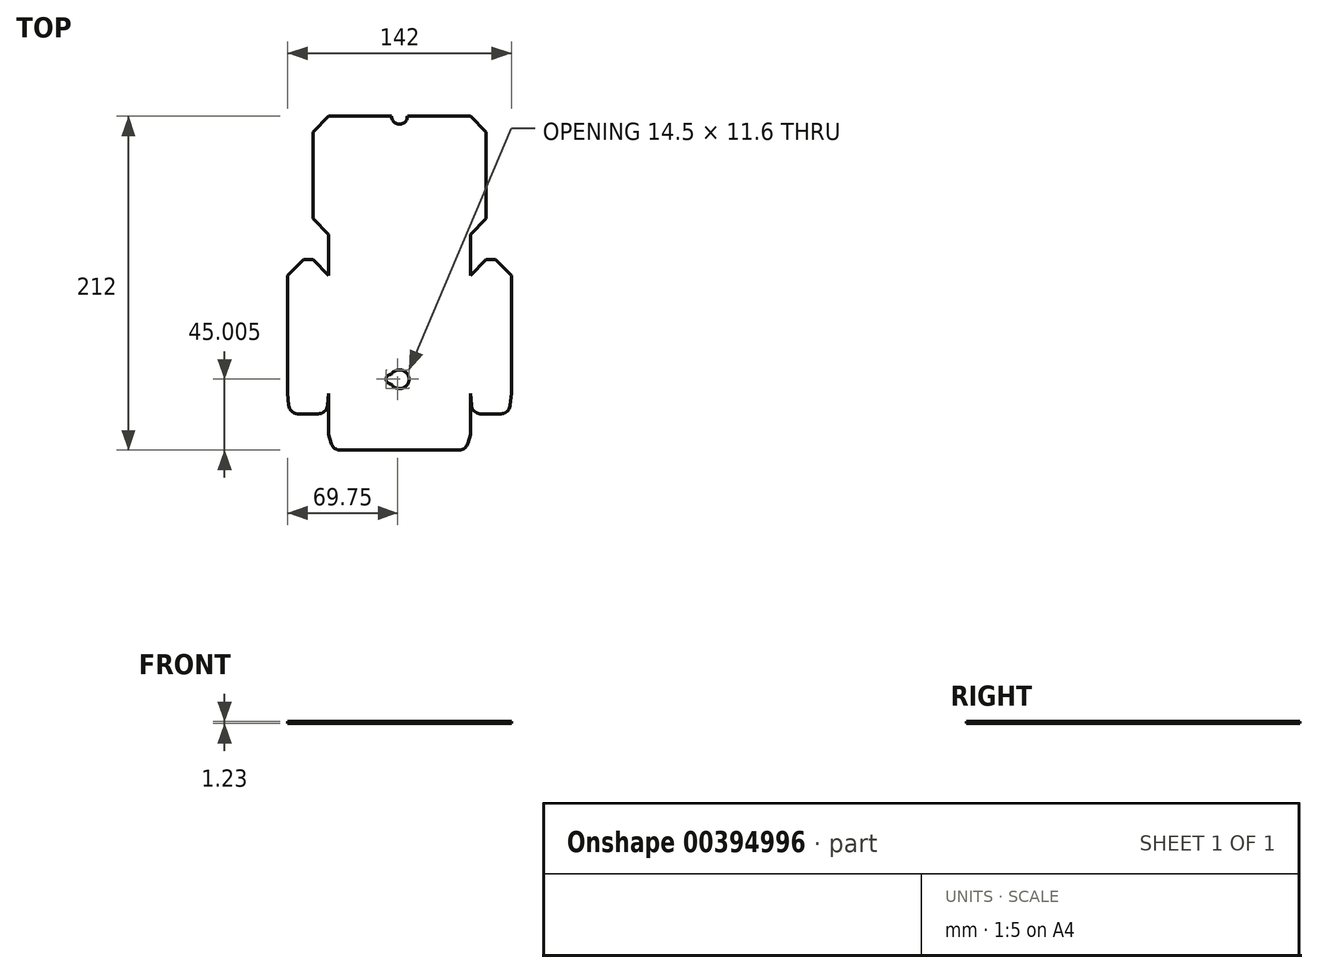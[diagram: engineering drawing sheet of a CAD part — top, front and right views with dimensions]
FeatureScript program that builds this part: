
annotation { "Feature Type Name" : "Feature", "Feature Type Description" : "" }
export const myFeature = defineFeature(function(context is Context, id is Id, definition is map)
    precondition{}
    {
        {
            var Q0;
            Q0=qCreatedBy(makeId("Top.planeOp"),FACE);
            var sketch = newSketch(context, id + "F0", { "sketchPlane" : qUnion([Q0])});
            skLineSegment(sketch, "E0", {"start": v(-70.76, -47.2) * mm, "end": v(-70.1, -54.72) * mm});
            skLineSegment(sketch, "E1", {"start": v(-70.1, -54.72) * mm, "end": v(-69.92, -55.75) * mm});
            skLineSegment(sketch, "E2", {"start": v(-69.92, -55.75) * mm, "end": v(-69.56, -56.73) * mm});
            skLineSegment(sketch, "E3", {"start": v(-69.56, -56.73) * mm, "end": v(-69.04, -57.64) * mm});
            skLineSegment(sketch, "E4", {"start": v(-69.04, -57.64) * mm, "end": v(-68.37, -58.44) * mm});
            skLineSegment(sketch, "E5", {"start": v(-68.37, -58.44) * mm, "end": v(-67.57, -59.11) * mm});
            skLineSegment(sketch, "E6", {"start": v(-67.57, -59.11) * mm, "end": v(-66.66, -59.63) * mm});
            skLineSegment(sketch, "E7", {"start": v(-66.66, -59.63) * mm, "end": v(-65.68, -60) * mm});
            skLineSegment(sketch, "E8", {"start": v(-65.68, -60) * mm, "end": v(-64.65, -60.17) * mm});
            skLineSegment(sketch, "E9", {"start": v(-64.65, -60.17) * mm, "end": v(-64.12, -60.2) * mm});
            skLineSegment(sketch, "E10", {"start": v(-64.12, -60.2) * mm, "end": v(-51.4, -60.2) * mm});
            skLineSegment(sketch, "E11", {"start": v(-51.4, -60.2) * mm, "end": v(-50.35, -60.1) * mm});
            skLineSegment(sketch, "E12", {"start": v(-50.35, -60.1) * mm, "end": v(-49.34, -59.83) * mm});
            skLineSegment(sketch, "E13", {"start": v(-49.34, -59.83) * mm, "end": v(-48.4, -59.4) * mm});
            skLineSegment(sketch, "E14", {"start": v(-48.4, -59.4) * mm, "end": v(-47.54, -58.8) * mm});
            skLineSegment(sketch, "E15", {"start": v(-47.54, -58.8) * mm, "end": v(-46.8, -58.05) * mm});
            skLineSegment(sketch, "E16", {"start": v(-46.8, -58.05) * mm, "end": v(-46.2, -57.2) * mm});
            skLineSegment(sketch, "E17", {"start": v(-46.2, -57.2) * mm, "end": v(-45.76, -56.25) * mm});
            skLineSegment(sketch, "E18", {"start": v(-45.76, -56.25) * mm, "end": v(-45.49, -55.24) * mm});
            skLineSegment(sketch, "E19", {"start": v(-45.49, -55.24) * mm, "end": v(-45.42, -54.72) * mm});
            skLineSegment(sketch, "E20", {"start": v(-45.42, -54.72) * mm, "end": v(-44.76, -47.2) * mm});
            skLineSegment(sketch, "E21", {"start": v(-44.76, -47.2) * mm, "end": v(-44.76, -73.2) * mm});
            skLineSegment(sketch, "E22", {"start": v(-44.76, -73.2) * mm, "end": v(-43.27, -78.75) * mm});
            skLineSegment(sketch, "E23", {"start": v(-43.27, -78.75) * mm, "end": v(-42.91, -79.73) * mm});
            skLineSegment(sketch, "E24", {"start": v(-42.91, -79.73) * mm, "end": v(-42.4, -80.64) * mm});
            skLineSegment(sketch, "E25", {"start": v(-42.4, -80.64) * mm, "end": v(-41.72, -81.44) * mm});
            skLineSegment(sketch, "E26", {"start": v(-41.72, -81.44) * mm, "end": v(-40.92, -82.11) * mm});
            skLineSegment(sketch, "E27", {"start": v(-40.92, -82.11) * mm, "end": v(-40.01, -82.63) * mm});
            skLineSegment(sketch, "E28", {"start": v(-40.01, -82.63) * mm, "end": v(-39.03, -83) * mm});
            skLineSegment(sketch, "E29", {"start": v(-39.03, -83) * mm, "end": v(-38, -83.17) * mm});
            skLineSegment(sketch, "E30", {"start": v(-38, -83.17) * mm, "end": v(-37.48, -83.2) * mm});
            skLineSegment(sketch, "E31", {"start": v(-37.48, -83.2) * mm, "end": v(37.96, -83.2) * mm});
            skLineSegment(sketch, "E32", {"start": v(37.96, -83.2) * mm, "end": v(39, -83.1) * mm});
            skLineSegment(sketch, "E33", {"start": v(39, -83.1) * mm, "end": v(40, -82.83) * mm});
            skLineSegment(sketch, "E34", {"start": v(40, -82.83) * mm, "end": v(40.96, -82.4) * mm});
            skLineSegment(sketch, "E35", {"start": v(40.96, -82.4) * mm, "end": v(41.81, -81.8) * mm});
            skLineSegment(sketch, "E36", {"start": v(41.81, -81.8) * mm, "end": v(42.55, -81.05) * mm});
            skLineSegment(sketch, "E37", {"start": v(42.55, -81.05) * mm, "end": v(43.15, -80.2) * mm});
            skLineSegment(sketch, "E38", {"start": v(43.15, -80.2) * mm, "end": v(43.6, -79.25) * mm});
            skLineSegment(sketch, "E39", {"start": v(43.6, -79.25) * mm, "end": v(43.75, -78.75) * mm});
            skLineSegment(sketch, "E40", {"start": v(43.75, -78.75) * mm, "end": v(45.24, -73.2) * mm});
            skLineSegment(sketch, "E41", {"start": v(45.24, -73.2) * mm, "end": v(45.24, -47.2) * mm});
            skLineSegment(sketch, "E42", {"start": v(45.24, -47.2) * mm, "end": v(45.9, -54.72) * mm});
            skLineSegment(sketch, "E43", {"start": v(45.9, -54.72) * mm, "end": v(46.08, -55.75) * mm});
            skLineSegment(sketch, "E44", {"start": v(46.08, -55.75) * mm, "end": v(46.44, -56.73) * mm});
            skLineSegment(sketch, "E45", {"start": v(46.44, -56.73) * mm, "end": v(46.96, -57.64) * mm});
            skLineSegment(sketch, "E46", {"start": v(46.96, -57.64) * mm, "end": v(47.63, -58.44) * mm});
            skLineSegment(sketch, "E47", {"start": v(47.63, -58.44) * mm, "end": v(48.43, -59.11) * mm});
            skLineSegment(sketch, "E48", {"start": v(48.43, -59.11) * mm, "end": v(49.34, -59.63) * mm});
            skLineSegment(sketch, "E49", {"start": v(49.34, -59.63) * mm, "end": v(50.32, -60) * mm});
            skLineSegment(sketch, "E50", {"start": v(50.32, -60) * mm, "end": v(51.35, -60.17) * mm});
            skLineSegment(sketch, "E51", {"start": v(51.35, -60.17) * mm, "end": v(51.88, -60.2) * mm});
            skLineSegment(sketch, "E52", {"start": v(51.88, -60.2) * mm, "end": v(64.6, -60.2) * mm});
            skLineSegment(sketch, "E53", {"start": v(64.6, -60.2) * mm, "end": v(65.65, -60.1) * mm});
            skLineSegment(sketch, "E54", {"start": v(65.65, -60.1) * mm, "end": v(66.66, -59.83) * mm});
            skLineSegment(sketch, "E55", {"start": v(66.66, -59.83) * mm, "end": v(67.6, -59.4) * mm});
            skLineSegment(sketch, "E56", {"start": v(67.6, -59.4) * mm, "end": v(68.46, -58.8) * mm});
            skLineSegment(sketch, "E57", {"start": v(68.46, -58.8) * mm, "end": v(69.2, -58.05) * mm});
            skLineSegment(sketch, "E58", {"start": v(69.2, -58.05) * mm, "end": v(69.8, -57.2) * mm});
            skLineSegment(sketch, "E59", {"start": v(69.8, -57.2) * mm, "end": v(70.24, -56.25) * mm});
            skLineSegment(sketch, "E60", {"start": v(70.24, -56.25) * mm, "end": v(70.51, -55.24) * mm});
            skLineSegment(sketch, "E61", {"start": v(70.51, -55.24) * mm, "end": v(70.58, -54.72) * mm});
            skLineSegment(sketch, "E62", {"start": v(70.58, -54.72) * mm, "end": v(71.24, -47.2) * mm});
            skLineSegment(sketch, "E63", {"start": v(71.24, -47.2) * mm, "end": v(71.24, 27.8) * mm});
            skLineSegment(sketch, "E64", {"start": v(71.24, 27.8) * mm, "end": v(61.24, 37.8) * mm});
            skLineSegment(sketch, "E65", {"start": v(61.24, 37.8) * mm, "end": v(55.24, 37.8) * mm});
            skLineSegment(sketch, "E66", {"start": v(55.24, 37.8) * mm, "end": v(45.24, 27.8) * mm});
            skLineSegment(sketch, "E67", {"start": v(45.24, 27.8) * mm, "end": v(45.24, 53.8) * mm});
            skLineSegment(sketch, "E68", {"start": v(45.24, 53.8) * mm, "end": v(55.24, 63.8) * mm});
            skLineSegment(sketch, "E69", {"start": v(55.24, 63.8) * mm, "end": v(55.24, 118.8) * mm});
            skLineSegment(sketch, "E70", {"start": v(55.24, 118.8) * mm, "end": v(45.24, 128.8) * mm});
            skLineSegment(sketch, "E71", {"start": v(45.24, 128.8) * mm, "end": v(5.24, 128.8) * mm});
            skLineSegment(sketch, "E72", {"start": v(5.24, 128.8) * mm, "end": v(5.16, 127.94) * mm});
            skLineSegment(sketch, "E73", {"start": v(5.16, 127.94) * mm, "end": v(4.94, 127.1) * mm});
            skLineSegment(sketch, "E74", {"start": v(4.94, 127.1) * mm, "end": v(4.57, 126.3) * mm});
            skLineSegment(sketch, "E75", {"start": v(4.57, 126.3) * mm, "end": v(4.07, 125.6) * mm});
            skLineSegment(sketch, "E76", {"start": v(4.07, 125.6) * mm, "end": v(3.45, 124.97) * mm});
            skLineSegment(sketch, "E77", {"start": v(3.45, 124.97) * mm, "end": v(2.74, 124.47) * mm});
            skLineSegment(sketch, "E78", {"start": v(2.74, 124.47) * mm, "end": v(1.95, 124.1) * mm});
            skLineSegment(sketch, "E79", {"start": v(1.95, 124.1) * mm, "end": v(1.1, 123.88) * mm});
            skLineSegment(sketch, "E80", {"start": v(1.1, 123.88) * mm, "end": v(0.24, 123.8) * mm});
            skLineSegment(sketch, "E81", {"start": v(0.24, 123.8) * mm, "end": v(-0.63, 123.88) * mm});
            skLineSegment(sketch, "E82", {"start": v(-0.63, 123.88) * mm, "end": v(-1.47, 124.1) * mm});
            skLineSegment(sketch, "E83", {"start": v(-1.47, 124.1) * mm, "end": v(-2.26, 124.47) * mm});
            skLineSegment(sketch, "E84", {"start": v(-2.26, 124.47) * mm, "end": v(-2.97, 124.97) * mm});
            skLineSegment(sketch, "E85", {"start": v(-2.97, 124.97) * mm, "end": v(-3.6, 125.6) * mm});
            skLineSegment(sketch, "E86", {"start": v(-3.6, 125.6) * mm, "end": v(-4.1, 126.3) * mm});
            skLineSegment(sketch, "E87", {"start": v(-4.1, 126.3) * mm, "end": v(-4.46, 127.1) * mm});
            skLineSegment(sketch, "E88", {"start": v(-4.46, 127.1) * mm, "end": v(-4.68, 127.94) * mm});
            skLineSegment(sketch, "E89", {"start": v(-4.68, 127.94) * mm, "end": v(-4.76, 128.8) * mm});
            skLineSegment(sketch, "E90", {"start": v(-4.76, 128.8) * mm, "end": v(-44.76, 128.8) * mm});
            skLineSegment(sketch, "E91", {"start": v(-44.76, 128.8) * mm, "end": v(-54.76, 118.8) * mm});
            skLineSegment(sketch, "E92", {"start": v(-54.76, 118.8) * mm, "end": v(-54.76, 63.8) * mm});
            skLineSegment(sketch, "E93", {"start": v(-54.76, 63.8) * mm, "end": v(-44.76, 53.8) * mm});
            skLineSegment(sketch, "E94", {"start": v(-44.76, 53.8) * mm, "end": v(-44.76, 27.8) * mm});
            skLineSegment(sketch, "E95", {"start": v(-44.76, 27.8) * mm, "end": v(-54.76, 37.8) * mm});
            skLineSegment(sketch, "E96", {"start": v(-54.76, 37.8) * mm, "end": v(-60.76, 37.8) * mm});
            skLineSegment(sketch, "E97", {"start": v(-60.76, 37.8) * mm, "end": v(-70.76, 27.8) * mm});
            skLineSegment(sketch, "E98", {"start": v(-70.76, 27.8) * mm, "end": v(-70.76, -47.2) * mm});
            skLineSegment(sketch, "E99", {"start": v(-70.76, 27.8) * mm, "end": v(-44.76, 27.8) * mm, "construction": true});
            skLineSegment(sketch, "E100", {"start": v(45.24, -47.2) * mm, "end": v(71.24, -47.2) * mm, "construction": true});
            skLineSegment(sketch, "E101", {"start": v(45.24, 27.8) * mm, "end": v(71.24, 27.8) * mm, "construction": true});
            skLineSegment(sketch, "E102", {"start": v(-70.76, -47.2) * mm, "end": v(-44.76, -47.2) * mm, "construction": true});
            skLineSegment(sketch, "E103", {"start": v(-44.76, 27.8) * mm, "end": v(45.24, 27.8) * mm, "construction": true});
            skLineSegment(sketch, "E104", {"start": v(-44.76, 53.8) * mm, "end": v(45.24, 53.8) * mm, "construction": true});
            skLineSegment(sketch, "E105", {"start": v(-44.76, -73.2) * mm, "end": v(45.24, -73.2) * mm, "construction": true});
            skLineSegment(sketch, "E106", {"start": v(-44.76, -47.2) * mm, "end": v(45.24, -47.2) * mm, "construction": true});
            skLineSegment(sketch, "E107", {"start": v(-44.76, 53.8) * mm, "end": v(-44.76, 128.8) * mm, "construction": true});
            skLineSegment(sketch, "E108", {"start": v(45.24, -47.2) * mm, "end": v(45.24, 27.8) * mm, "construction": true});
            skLineSegment(sketch, "E109", {"start": v(45.24, 53.8) * mm, "end": v(45.24, 128.8) * mm, "construction": true});
            skLineSegment(sketch, "E110", {"start": v(-44.76, -47.2) * mm, "end": v(-44.76, 27.8) * mm, "construction": true});
            skSolve(sketch);
        }
        {
            var Q0;
            Q0 = qSketchRegion(id + "F0", true);
            extrude(context, id + "F1", {"entities" : qUnion([Q0]), "depth" : 1.23 * mm});
        }
        {
            var Q0;
            Q0=makeQuery(id+"F1.opExtrude","CAP_FACE",FACE,{"disambiguationData":[OSD([sQuery(id+"F0.wireOp",EDGE,"E0"),sQuery(id+"F0.wireOp",EDGE,"E1"),sQuery(id+"F0.wireOp",EDGE,"E2"),sQuery(id+"F0.wireOp",EDGE,"E3"),sQuery(id+"F0.wireOp",EDGE,"E4"),sQuery(id+"F0.wireOp",EDGE,"E5"),sQuery(id+"F0.wireOp",EDGE,"E6"),sQuery(id+"F0.wireOp",EDGE,"E7"),sQuery(id+"F0.wireOp",EDGE,"E8"),sQuery(id+"F0.wireOp",EDGE,"E9"),sQuery(id+"F0.wireOp",EDGE,"E10"),sQuery(id+"F0.wireOp",EDGE,"E11"),sQuery(id+"F0.wireOp",EDGE,"E12"),sQuery(id+"F0.wireOp",EDGE,"E13"),sQuery(id+"F0.wireOp",EDGE,"E14"),sQuery(id+"F0.wireOp",EDGE,"E15"),sQuery(id+"F0.wireOp",EDGE,"E16"),sQuery(id+"F0.wireOp",EDGE,"E17"),sQuery(id+"F0.wireOp",EDGE,"E18"),sQuery(id+"F0.wireOp",EDGE,"E19"),sQuery(id+"F0.wireOp",EDGE,"E20"),sQuery(id+"F0.wireOp",EDGE,"E21"),sQuery(id+"F0.wireOp",EDGE,"E22"),sQuery(id+"F0.wireOp",EDGE,"E23"),sQuery(id+"F0.wireOp",EDGE,"E24"),sQuery(id+"F0.wireOp",EDGE,"E25"),sQuery(id+"F0.wireOp",EDGE,"E26"),sQuery(id+"F0.wireOp",EDGE,"E27"),sQuery(id+"F0.wireOp",EDGE,"E28"),sQuery(id+"F0.wireOp",EDGE,"E29"),sQuery(id+"F0.wireOp",EDGE,"E30"),sQuery(id+"F0.wireOp",EDGE,"E31"),sQuery(id+"F0.wireOp",EDGE,"E32"),sQuery(id+"F0.wireOp",EDGE,"E33"),sQuery(id+"F0.wireOp",EDGE,"E34"),sQuery(id+"F0.wireOp",EDGE,"E35"),sQuery(id+"F0.wireOp",EDGE,"E36"),sQuery(id+"F0.wireOp",EDGE,"E37"),sQuery(id+"F0.wireOp",EDGE,"E38"),sQuery(id+"F0.wireOp",EDGE,"E39"),sQuery(id+"F0.wireOp",EDGE,"E40"),sQuery(id+"F0.wireOp",EDGE,"E41"),sQuery(id+"F0.wireOp",EDGE,"E42"),sQuery(id+"F0.wireOp",EDGE,"E43"),sQuery(id+"F0.wireOp",EDGE,"E44"),sQuery(id+"F0.wireOp",EDGE,"E45"),sQuery(id+"F0.wireOp",EDGE,"E46"),sQuery(id+"F0.wireOp",EDGE,"E47"),sQuery(id+"F0.wireOp",EDGE,"E48"),sQuery(id+"F0.wireOp",EDGE,"E49"),sQuery(id+"F0.wireOp",EDGE,"E50"),sQuery(id+"F0.wireOp",EDGE,"E51"),sQuery(id+"F0.wireOp",EDGE,"E52"),sQuery(id+"F0.wireOp",EDGE,"E53"),sQuery(id+"F0.wireOp",EDGE,"E54"),sQuery(id+"F0.wireOp",EDGE,"E55"),sQuery(id+"F0.wireOp",EDGE,"E56"),sQuery(id+"F0.wireOp",EDGE,"E57"),sQuery(id+"F0.wireOp",EDGE,"E58"),sQuery(id+"F0.wireOp",EDGE,"E59"),sQuery(id+"F0.wireOp",EDGE,"E60"),sQuery(id+"F0.wireOp",EDGE,"E61"),sQuery(id+"F0.wireOp",EDGE,"E62"),sQuery(id+"F0.wireOp",EDGE,"E63"),sQuery(id+"F0.wireOp",EDGE,"E64"),sQuery(id+"F0.wireOp",EDGE,"E65"),sQuery(id+"F0.wireOp",EDGE,"E66"),sQuery(id+"F0.wireOp",EDGE,"E67"),sQuery(id+"F0.wireOp",EDGE,"E68"),sQuery(id+"F0.wireOp",EDGE,"E69"),sQuery(id+"F0.wireOp",EDGE,"E70"),sQuery(id+"F0.wireOp",EDGE,"E71"),sQuery(id+"F0.wireOp",EDGE,"E72"),sQuery(id+"F0.wireOp",EDGE,"E73"),sQuery(id+"F0.wireOp",EDGE,"E74"),sQuery(id+"F0.wireOp",EDGE,"E75"),sQuery(id+"F0.wireOp",EDGE,"E76"),sQuery(id+"F0.wireOp",EDGE,"E77"),sQuery(id+"F0.wireOp",EDGE,"E78"),sQuery(id+"F0.wireOp",EDGE,"E79"),sQuery(id+"F0.wireOp",EDGE,"E80"),sQuery(id+"F0.wireOp",EDGE,"E81"),sQuery(id+"F0.wireOp",EDGE,"E82"),sQuery(id+"F0.wireOp",EDGE,"E83"),sQuery(id+"F0.wireOp",EDGE,"E84"),sQuery(id+"F0.wireOp",EDGE,"E85"),sQuery(id+"F0.wireOp",EDGE,"E86"),sQuery(id+"F0.wireOp",EDGE,"E87"),sQuery(id+"F0.wireOp",EDGE,"E88"),sQuery(id+"F0.wireOp",EDGE,"E89"),sQuery(id+"F0.wireOp",EDGE,"E90"),sQuery(id+"F0.wireOp",EDGE,"E91"),sQuery(id+"F0.wireOp",EDGE,"E92"),sQuery(id+"F0.wireOp",EDGE,"E93"),sQuery(id+"F0.wireOp",EDGE,"E94"),sQuery(id+"F0.wireOp",EDGE,"E95"),sQuery(id+"F0.wireOp",EDGE,"E96"),sQuery(id+"F0.wireOp",EDGE,"E97"),sQuery(id+"F0.wireOp",EDGE,"E98")])],"isStart":false});
            var sketch = newSketch(context, id + "F2", { "sketchPlane" : qUnion([Q0])});
            skLineSegment(sketch, "E111.bottom", {"start": v(-16.26, -44.2) * mm, "end": v(6.24, -44.2) * mm, "construction": true});
            skLineSegment(sketch, "E111.top", {"start": v(-16.26, -32.2) * mm, "end": v(6.24, -32.2) * mm, "construction": true});
            skLineSegment(sketch, "E111.left", {"start": v(-16.26, -44.2) * mm, "end": v(-16.26, -32.2) * mm, "construction": true});
            skLineSegment(sketch, "E111.right", {"start": v(6.24, -44.2) * mm, "end": v(6.24, -32.2) * mm, "construction": true});
            skArc(sketch, "E112", {"start": v(-4.96, -41.18) * mm, "mid": v(6.24, -38.2) * mm, "end": v(-4.96, -35.2) * mm});
            skArc(sketch, "E113", {"start": v(-4.96, -35.2) * mm, "mid": v(-8.26, -38.2) * mm, "end": v(-4.96, -41.18) * mm});
            skLineSegment(sketch, "E114", {"start": v(45.24, -38.2) * mm, "end": v(-44.76, -38.2) * mm, "construction": true});
            skLineSegment(sketch, "E115.0", {"start": v(-18.76, -29.7) * mm, "end": v(8.74, -29.7) * mm, "construction": true});
            skLineSegment(sketch, "E115.1", {"start": v(-18.76, -46.7) * mm, "end": v(-18.76, -29.7) * mm, "construction": true});
            skLineSegment(sketch, "E115.2", {"start": v(-18.76, -46.7) * mm, "end": v(8.74, -46.7) * mm, "construction": true});
            skLineSegment(sketch, "E115.3", {"start": v(8.74, -46.7) * mm, "end": v(8.74, -29.7) * mm, "construction": true});
            skSolve(sketch);
        }
        {
            var Q0;
            Q0 = qSketchRegion(id + "F2", true);
            extrude(context, id + "F3", {"entities" : qUnion([Q0]), "operationType" : NewBodyOperationType.REMOVE, "endBound" : BoundingType.THROUGH_ALL, "oppositeDirection" : true, "depth" : 25 * mm});
        }
    });
